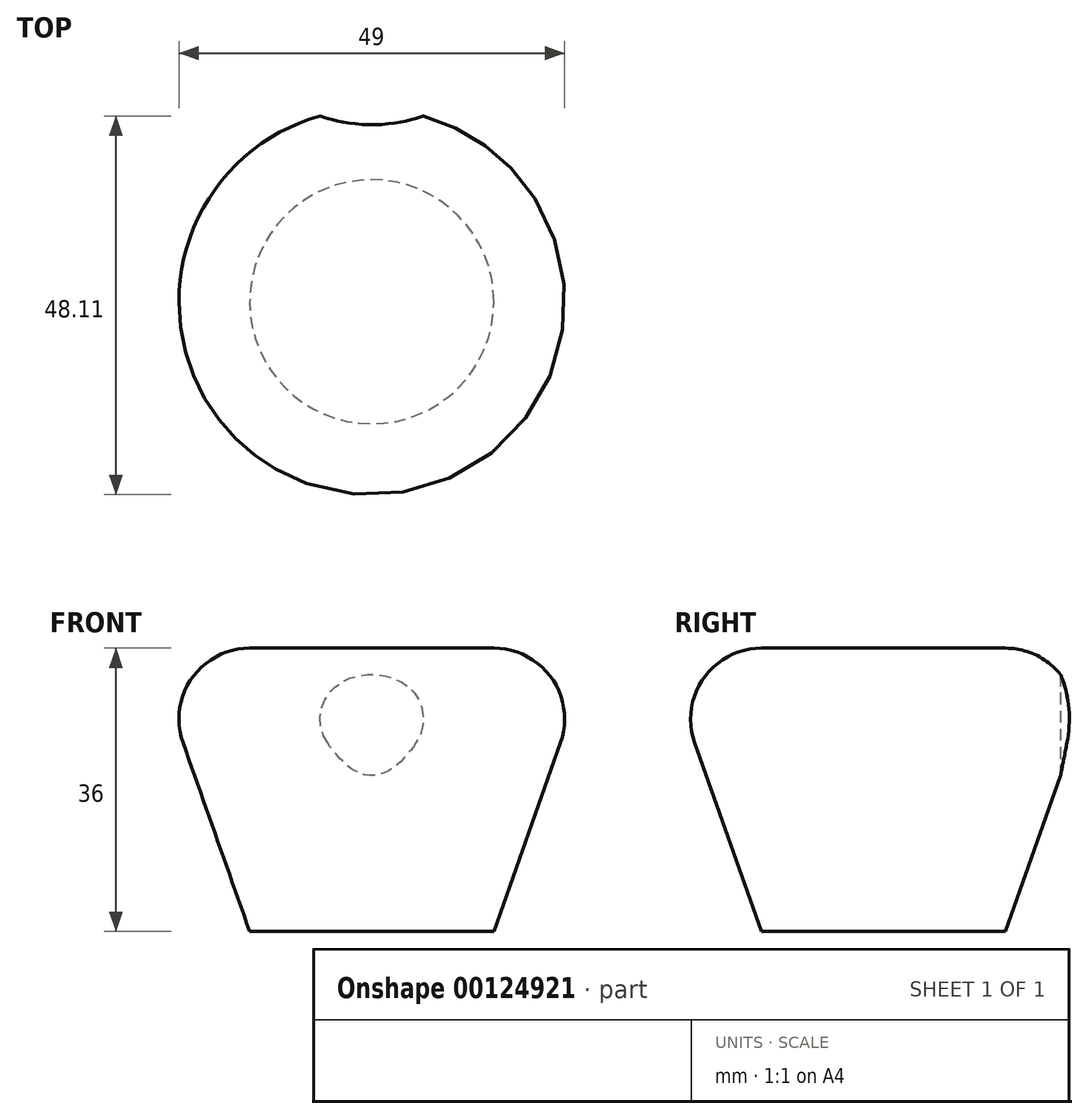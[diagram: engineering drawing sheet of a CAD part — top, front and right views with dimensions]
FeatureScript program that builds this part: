
annotation { "Feature Type Name" : "Feature", "Feature Type Description" : "" }
export const myFeature = defineFeature(function(context is Context, id is Id, definition is map)
    precondition{}
    {
        {
            var Q0;
            Q0=qCreatedBy(makeId("Front.planeOp"),FACE);
            var sketch = newSketch(context, id + "F0", { "sketchPlane" : qUnion([Q0])});
            skLineSegment(sketch, "E0", {"start": v(0, 0) * mm, "end": v(0, 36) * mm});
            skLineSegment(sketch, "E1", {"start": v(0, 36) * mm, "end": v(-28.23, 36) * mm});
            skLineSegment(sketch, "E2", {"start": v(-28.23, 36) * mm, "end": v(-15.5, 0) * mm});
            skLineSegment(sketch, "E3", {"start": v(-15.5, 0) * mm, "end": v(0, 0) * mm});
            skArc(sketch, "E4", {"start": v(-15.5, 36) * mm, "mid": v(-22.85, 32.2) * mm, "end": v(-23.99, 24) * mm});
            skLineSegment(sketch, "E5", {"start": v(-24.5, 42.5) * mm, "end": v(-24.5, 17.9) * mm});
            skSolve(sketch);
        }
        {
            var Q0;
            {var subQ5=sQuery(id+"F0.wireOp",EDGE,"E0");Q0=makeQuery(id+"F0.imprint","IMPRINT",FACE,{"disambiguationData":[TD([[makeQuery(id+"F0.imprint","IMPRINT",EDGE,{"derivedFrom":subQ5}),1.0]])]});}
            var Q1;
            Q1=sQuery(id+"F0.wireOp",EDGE,"E0");
            revolve(context, id + "F1", {"entities" : qUnion([Q0]), "axis" : qUnion([Q1]), "revolveType" : RevolveType.FULL});
        }
        {
            var Q0;
            Q0=qCreatedBy(makeId("Top.planeOp"),FACE);
            var sketch = newSketch(context, id + "F2", { "sketchPlane" : qUnion([Q0])});
            skArc(sketch, "E6", {"start": v(-11.5, 26.14) * mm, "mid": v(-1.13, 22.53) * mm, "end": v(9.57, 24.94) * mm});
            skLineSegment(sketch, "E7", {"start": v(0, 42.5) * mm, "end": v(-11.5, 26.14) * mm});
            skLineSegment(sketch, "E8", {"start": v(9.57, 24.94) * mm, "end": v(0, 42.5) * mm});
            skLineSegment(sketch, "E9", {"start": v(0, 42.5) * mm, "end": v(0, 0) * mm});
            skSolve(sketch);
        }
        {
            var Q0;
            {var subQ0=sQuery(id+"F2.wireOp",EDGE,"E7");Q0=makeQuery(id+"F2.imprint","IMPRINT",FACE,{"disambiguationData":[TD([[makeQuery(id+"F2.imprint","IMPRINT",EDGE,{"derivedFrom":subQ0}),1.0]])]});}
            var Q1;
            {var subQ0=sQuery(id+"F2.wireOp",EDGE,"E8");Q1=makeQuery(id+"F2.imprint","IMPRINT",FACE,{"disambiguationData":[TD([[makeQuery(id+"F2.imprint","IMPRINT",EDGE,{"derivedFrom":subQ0}),1.0]])]});}
            extrude(context, id + "F3", {"entities" : qUnion([Q0, Q1]), "operationType" : NewBodyOperationType.REMOVE, "endBound" : BoundingType.THROUGH_ALL, "depth" : 25 * mm});
        }
    });
